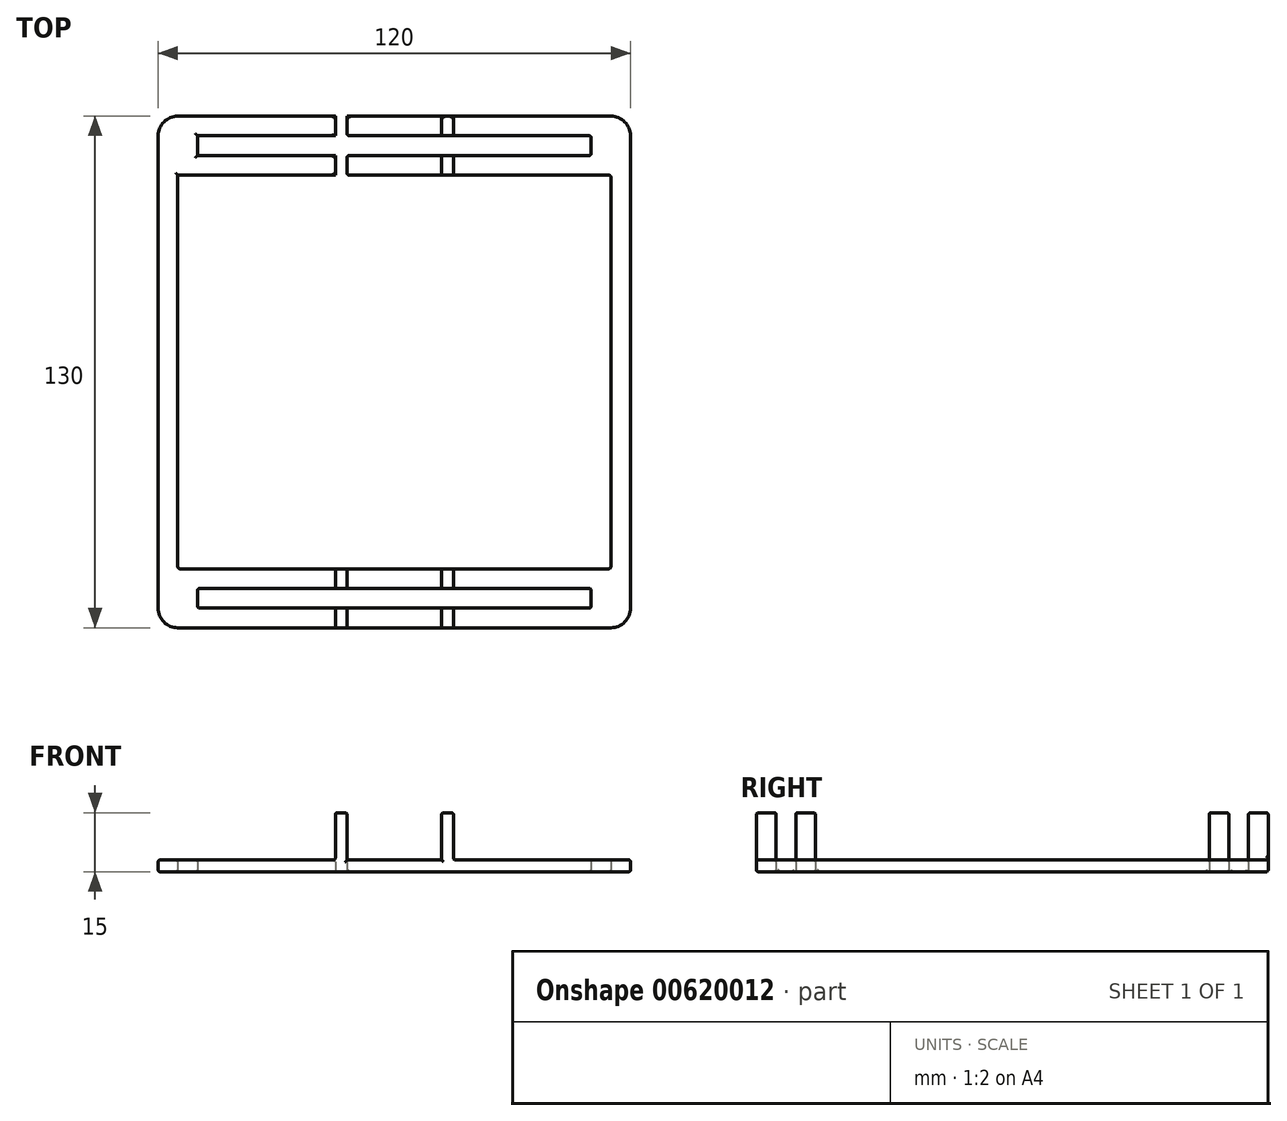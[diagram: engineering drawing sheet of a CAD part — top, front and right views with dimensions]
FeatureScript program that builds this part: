
annotation { "Feature Type Name" : "Feature", "Feature Type Description" : "" }
export const myFeature = defineFeature(function(context is Context, id is Id, definition is map)
    precondition{}
    {
        {
            var Q0;
            Q0=qCreatedBy(makeId("Top.planeOp"),FACE);
            var sketch = newSketch(context, id + "F0", { "sketchPlane" : qUnion([Q0])});
            skLineSegment(sketch, "E0.bottom", {"start": v(-50, 55) * mm, "end": v(50, 55) * mm});
            skLineSegment(sketch, "E0.left", {"start": v(-55, 50) * mm, "end": v(-55, -50) * mm});
            skLineSegment(sketch, "E0.right", {"start": v(55, 50) * mm, "end": v(55, -50) * mm});
            skPoint(sketch, "E0.middle", {"position": v(0, 0) * mm});
            skLineSegment(sketch, "E1.left", {"start": v(-60, 55) * mm, "end": v(-60, -55) * mm});
            skLineSegment(sketch, "E1.right", {"start": v(60, 55) * mm, "end": v(60, -55) * mm});
            skPoint(sketch, "E2.visualSharp", {"position": v(-55, 55) * mm});
            skPoint(sketch, "E3.visualSharp", {"position": v(-60, 60) * mm});
            skPoint(sketch, "E4.visualSharp", {"position": v(55, 55) * mm});
            skPoint(sketch, "E5.visualSharp", {"position": v(60, 60) * mm});
            skPoint(sketch, "E6.visualSharp", {"position": v(55, -55) * mm});
            skPoint(sketch, "E7.visualSharp", {"position": v(60, -60) * mm});
            skPoint(sketch, "E8.visualSharp", {"position": v(-55, -55) * mm});
            skPoint(sketch, "E9.visualSharp", {"position": v(-60, -60) * mm});
            skLineSegment(sketch, "E10", {"start": v(-55, 50) * mm, "end": v(55, 50) * mm});
            skLineSegment(sketch, "E11", {"start": v(-50, 60) * mm, "end": v(-50, 55) * mm});
            skLineSegment(sketch, "E12", {"start": v(50, 60) * mm, "end": v(50, 55) * mm});
            skPoint(sketch, "E13.bottom.end.orphan", {"position": v(15, 55) * mm});
            skPoint(sketch, "E13.bottom.start.orphan", {"position": v(-15, 55) * mm});
            skPoint(sketch, "E13.top.end.orphan", {"position": v(0, 60) * mm});
            skPoint(sketch, "E14.orphan", {"position": v(-15, 60) * mm});
            skPoint(sketch, "E15.orphan", {"position": v(15, 60) * mm});
            skPoint(sketch, "E16.MirrorCS.end.orphan", {"position": v(-15, -60) * mm});
            skPoint(sketch, "E16.MirrorCS.start.orphan", {"position": v(-15, -55) * mm});
            skPoint(sketch, "E17.MirrorCS.end.orphan", {"position": v(15, -60) * mm});
            skPoint(sketch, "E0.top.start.orphan", {"position": v(15, -55) * mm});
            skPoint(sketch, "E1.bottom.start.orphan", {"position": v(-55, 60) * mm});
            skPoint(sketch, "E18.trimOffspring.end.orphan", {"position": v(55, 60) * mm});
            skLineSegment(sketch, "E19", {"start": v(-50, 60) * mm, "end": v(50, 60) * mm});
            skPoint(sketch, "E20", {"position": v(-55, 65) * mm});
            skLineSegment(sketch, "E21", {"start": v(-55, 65) * mm, "end": v(55, 65) * mm});
            skLineSegment(sketch, "E22", {"start": v(-60, 55) * mm, "end": v(-60, 60) * mm});
            skLineSegment(sketch, "E23", {"start": v(-60, 60) * mm, "end": v(-60, 65) * mm});
            skLineSegment(sketch, "E24", {"start": v(-60, 65) * mm, "end": v(-55, 65) * mm});
            skLineSegment(sketch, "E25", {"start": v(60, 55) * mm, "end": v(60, 60) * mm});
            skLineSegment(sketch, "E26", {"start": v(60, 60) * mm, "end": v(60, 65) * mm});
            skLineSegment(sketch, "E27", {"start": v(60, 65) * mm, "end": v(55, 65) * mm});
            skLineSegment(sketch, "E28.MirrorCS", {"start": v(-55, -50) * mm, "end": v(55, -50) * mm});
            skLineSegment(sketch, "E29.MirrorCS", {"start": v(-50, -55) * mm, "end": v(50, -55) * mm});
            skLineSegment(sketch, "E30.MirrorCS", {"start": v(-50, -60) * mm, "end": v(50, -60) * mm});
            skLineSegment(sketch, "E31.MirrorCS", {"start": v(-50, -60) * mm, "end": v(-50, -55) * mm});
            skLineSegment(sketch, "E32.MirrorCS", {"start": v(50, -60) * mm, "end": v(50, -55) * mm});
            skLineSegment(sketch, "E33.MirrorCS", {"start": v(60, -55) * mm, "end": v(60, -60) * mm});
            skLineSegment(sketch, "E34.MirrorCS", {"start": v(60, -60) * mm, "end": v(60, -65) * mm});
            skLineSegment(sketch, "E35.MirrorCS", {"start": v(60, -65) * mm, "end": v(55, -65) * mm});
            skLineSegment(sketch, "E36.MirrorCS", {"start": v(-55, -65) * mm, "end": v(55, -65) * mm});
            skLineSegment(sketch, "E37.MirrorCS", {"start": v(-60, -65) * mm, "end": v(-55, -65) * mm});
            skLineSegment(sketch, "E38.MirrorCS", {"start": v(-60, -60) * mm, "end": v(-60, -65) * mm});
            skLineSegment(sketch, "E39.MirrorCS", {"start": v(-60, -55) * mm, "end": v(-60, -60) * mm});
            skLineSegment(sketch, "E40.bottom", {"start": v(-15, 55) * mm, "end": v(-12, 55) * mm});
            skLineSegment(sketch, "E40.top", {"start": v(-15, 50) * mm, "end": v(-12, 50) * mm});
            skLineSegment(sketch, "E40.left", {"start": v(-15, 55) * mm, "end": v(-15, 50) * mm});
            skLineSegment(sketch, "E40.right", {"start": v(-12, 55) * mm, "end": v(-12, 50) * mm});
            skLineSegment(sketch, "E41.MirrorCS", {"start": v(12, 55) * mm, "end": v(12, 50) * mm});
            skLineSegment(sketch, "E42.MirrorCS", {"start": v(15, 55) * mm, "end": v(15, 50) * mm});
            skLineSegment(sketch, "E43.bottom", {"start": v(-15, 60) * mm, "end": v(-12, 60) * mm});
            skLineSegment(sketch, "E43.top", {"start": v(-15, 65) * mm, "end": v(-12, 65) * mm});
            skLineSegment(sketch, "E43.left", {"start": v(-15, 60) * mm, "end": v(-15, 65) * mm});
            skLineSegment(sketch, "E43.right", {"start": v(-12, 60) * mm, "end": v(-12, 65) * mm});
            skLineSegment(sketch, "E44.MirrorCS", {"start": v(12, 60) * mm, "end": v(12, 65) * mm});
            skLineSegment(sketch, "E45.MirrorCS", {"start": v(15, 60) * mm, "end": v(15, 65) * mm});
            skLineSegment(sketch, "E46.MirrorCS", {"start": v(-15, -55) * mm, "end": v(-15, -50) * mm});
            skLineSegment(sketch, "E47.MirrorCS", {"start": v(-12, -55) * mm, "end": v(-12, -50) * mm});
            skLineSegment(sketch, "E48.MirrorCS", {"start": v(-12, -60) * mm, "end": v(-12, -65) * mm});
            skLineSegment(sketch, "E49.MirrorCS", {"start": v(-15, -60) * mm, "end": v(-15, -65) * mm});
            skLineSegment(sketch, "E50.MirrorCS", {"start": v(12, -60) * mm, "end": v(12, -65) * mm});
            skLineSegment(sketch, "E51.MirrorCS", {"start": v(15, -60) * mm, "end": v(15, -65) * mm});
            skLineSegment(sketch, "E52.MirrorCS", {"start": v(15, -55) * mm, "end": v(15, -50) * mm});
            skLineSegment(sketch, "E53.MirrorCS", {"start": v(12, -55) * mm, "end": v(12, -50) * mm});
            skSolve(sketch);
        }
        {
            var Q0;
            Q0=makeQuery(id+"F0.imprint","IMPRINT",FACE,{"disambiguationData":[TD([[makeQuery(id+"F0.imprint","IMPRINT",EDGE,{"derivedFrom":sQuery(id+"F0.wireOp",EDGE,"E0.left")}),-1.0]])]});
            var Q1;
            Q1=makeQuery(id+"F0.imprint","IMPRINT",FACE,{"disambiguationData":[TD([[makeQuery(id+"F0.imprint","IMPRINT",EDGE,{"derivedFrom":sQuery(id+"F0.wireOp",EDGE,"E0.right")}),1.0]])]});
            extrude(context, id + "F1", {"entities" : qUnion([Q0, Q1]), "depth" : 3 * mm, "offsetDistance" : 25 * mm});
        }
        {
            var Q0;
            Q0=makeQuery(id+"F0.imprint","IMPRINT",FACE,{"disambiguationData":[TD([[makeQuery(id+"F0.imprint","IMPRINT",EDGE,{"derivedFrom":sQuery(id+"F0.wireOp",EDGE,"E43.bottom")}),1.0]])]});
            var Q1;
            Q1=makeQuery(id+"F0.imprint","IMPRINT",FACE,{"disambiguationData":[TD([[makeQuery(id+"F0.imprint","IMPRINT",EDGE,{"derivedFrom":sQuery(id+"F0.wireOp",EDGE,"E40.bottom")}),-1.0]])]});
            var Q2;
            {var subQ0=sQuery(id+"F0.wireOp",EDGE,"E41.MirrorCS");Q2=makeQuery(id+"F0.imprint","IMPRINT",FACE,{"disambiguationData":[TD([[makeQuery(id+"F0.imprint","IMPRINT",EDGE,{"derivedFrom":subQ0}),1.0]])]});}
            var Q3;
            {var subQ0=sQuery(id+"F0.wireOp",EDGE,"E44.MirrorCS");Q3=makeQuery(id+"F0.imprint","IMPRINT",FACE,{"disambiguationData":[TD([[makeQuery(id+"F0.imprint","IMPRINT",EDGE,{"derivedFrom":subQ0}),-1.0]])]});}
            var Q4;
            {var subQ0=sQuery(id+"F0.wireOp",EDGE,"E52.MirrorCS");Q4=makeQuery(id+"F0.imprint","IMPRINT",FACE,{"disambiguationData":[TD([[makeQuery(id+"F0.imprint","IMPRINT",EDGE,{"derivedFrom":subQ0}),1.0]])]});}
            var Q5;
            {var subQ0=sQuery(id+"F0.wireOp",EDGE,"E50.MirrorCS");Q5=makeQuery(id+"F0.imprint","IMPRINT",FACE,{"disambiguationData":[TD([[makeQuery(id+"F0.imprint","IMPRINT",EDGE,{"derivedFrom":subQ0}),1.0]])]});}
            var Q6;
            {var subQ0=sQuery(id+"F0.wireOp",EDGE,"E48.MirrorCS");Q6=makeQuery(id+"F0.imprint","IMPRINT",FACE,{"disambiguationData":[TD([[makeQuery(id+"F0.imprint","IMPRINT",EDGE,{"derivedFrom":subQ0}),-1.0]])]});}
            var Q7;
            {var subQ0=sQuery(id+"F0.wireOp",EDGE,"E46.MirrorCS");Q7=makeQuery(id+"F0.imprint","IMPRINT",FACE,{"disambiguationData":[TD([[makeQuery(id+"F0.imprint","IMPRINT",EDGE,{"derivedFrom":subQ0}),-1.0]])]});}
            extrude(context, id + "F2", {"entities" : qUnion([Q0, Q1, Q2, Q3, Q4, Q5, Q6, Q7]), "depth" : 15 * mm, "offsetDistance" : 25 * mm});
        }
        {
            var Q0;
            {var subQ0=sQuery(id+"F0.wireOp",EDGE,"E43.right");Q0=makeQuery(id+"F0.imprint","IMPRINT",FACE,{"disambiguationData":[TD([[makeQuery(id+"F0.imprint","IMPRINT",EDGE,{"derivedFrom":subQ0}),-1.0]])]});}
            var Q1;
            {var subQ0=sQuery(id+"F0.wireOp",EDGE,"E40.right");Q1=makeQuery(id+"F0.imprint","IMPRINT",FACE,{"disambiguationData":[TD([[makeQuery(id+"F0.imprint","IMPRINT",EDGE,{"derivedFrom":subQ0}),1.0]])]});}
            var Q2;
            {var subQ0=sQuery(id+"F0.wireOp",EDGE,"E47.MirrorCS");Q2=makeQuery(id+"F0.imprint","IMPRINT",FACE,{"disambiguationData":[TD([[makeQuery(id+"F0.imprint","IMPRINT",EDGE,{"derivedFrom":subQ0}),-1.0]])]});}
            var Q3;
            {var subQ0=sQuery(id+"F0.wireOp",EDGE,"E48.MirrorCS");Q3=makeQuery(id+"F0.imprint","IMPRINT",FACE,{"disambiguationData":[TD([[makeQuery(id+"F0.imprint","IMPRINT",EDGE,{"derivedFrom":subQ0}),1.0]])]});}
            extrude(context, id + "F3", {"entities" : qUnion([Q0, Q1, Q2, Q3]), "depth" : 3 * mm, "offsetDistance" : 25 * mm});
        }
        {
            var Q0;
            Q0=makeQuery(id+"F1.opExtrude","SWEPT_BODY",BODY,{"disambiguationData":[OSD([sQuery(id+"F0.wireOp",EDGE,"E0.bottom"),sQuery(id+"F0.wireOp",EDGE,"E0.left"),sQuery(id+"F0.wireOp",EDGE,"E1.left"),sQuery(id+"F0.wireOp",EDGE,"E10"),sQuery(id+"F0.wireOp",EDGE,"E11"),sQuery(id+"F0.wireOp",EDGE,"E19"),sQuery(id+"F0.wireOp",EDGE,"E21"),sQuery(id+"F0.wireOp",EDGE,"E22"),sQuery(id+"F0.wireOp",EDGE,"E23"),sQuery(id+"F0.wireOp",EDGE,"E24"),sQuery(id+"F0.wireOp",EDGE,"E28.MirrorCS"),sQuery(id+"F0.wireOp",EDGE,"E29.MirrorCS"),sQuery(id+"F0.wireOp",EDGE,"E30.MirrorCS"),sQuery(id+"F0.wireOp",EDGE,"E31.MirrorCS"),sQuery(id+"F0.wireOp",EDGE,"E36.MirrorCS"),sQuery(id+"F0.wireOp",EDGE,"E37.MirrorCS"),sQuery(id+"F0.wireOp",EDGE,"E38.MirrorCS"),sQuery(id+"F0.wireOp",EDGE,"E39.MirrorCS"),sQuery(id+"F0.wireOp",EDGE,"E40.left"),sQuery(id+"F0.wireOp",EDGE,"E43.left"),sQuery(id+"F0.wireOp",EDGE,"E46.MirrorCS"),sQuery(id+"F0.wireOp",EDGE,"E49.MirrorCS")])]});
            var Q1;
            Q1=makeQuery(id+"F1.opExtrude","SWEPT_BODY",BODY,{"disambiguationData":[OSD([sQuery(id+"F0.wireOp",EDGE,"E0.bottom"),sQuery(id+"F0.wireOp",EDGE,"E0.right"),sQuery(id+"F0.wireOp",EDGE,"E1.right"),sQuery(id+"F0.wireOp",EDGE,"E10"),sQuery(id+"F0.wireOp",EDGE,"E12"),sQuery(id+"F0.wireOp",EDGE,"E19"),sQuery(id+"F0.wireOp",EDGE,"E21"),sQuery(id+"F0.wireOp",EDGE,"E25"),sQuery(id+"F0.wireOp",EDGE,"E26"),sQuery(id+"F0.wireOp",EDGE,"E27"),sQuery(id+"F0.wireOp",EDGE,"E28.MirrorCS"),sQuery(id+"F0.wireOp",EDGE,"E29.MirrorCS"),sQuery(id+"F0.wireOp",EDGE,"E30.MirrorCS"),sQuery(id+"F0.wireOp",EDGE,"E32.MirrorCS"),sQuery(id+"F0.wireOp",EDGE,"E33.MirrorCS"),sQuery(id+"F0.wireOp",EDGE,"E34.MirrorCS"),sQuery(id+"F0.wireOp",EDGE,"E35.MirrorCS"),sQuery(id+"F0.wireOp",EDGE,"E36.MirrorCS"),sQuery(id+"F0.wireOp",EDGE,"E42.MirrorCS"),sQuery(id+"F0.wireOp",EDGE,"E45.MirrorCS"),sQuery(id+"F0.wireOp",EDGE,"E51.MirrorCS"),sQuery(id+"F0.wireOp",EDGE,"E52.MirrorCS")])]});
            var Q2;
            Q2=makeQuery(id+"F2.opExtrude","SWEPT_BODY",BODY,{"disambiguationData":[OSD([sQuery(id+"F0.wireOp",EDGE,"E0.bottom"),sQuery(id+"F0.wireOp",EDGE,"E10"),sQuery(id+"F0.wireOp",EDGE,"E41.MirrorCS"),sQuery(id+"F0.wireOp",EDGE,"E42.MirrorCS")])]});
            var Q3;
            Q3=makeQuery(id+"F2.opExtrude","SWEPT_BODY",BODY,{"disambiguationData":[OSD([sQuery(id+"F0.wireOp",EDGE,"E19"),sQuery(id+"F0.wireOp",EDGE,"E21"),sQuery(id+"F0.wireOp",EDGE,"E44.MirrorCS"),sQuery(id+"F0.wireOp",EDGE,"E45.MirrorCS")])]});
            var Q4;
            Q4=makeQuery(id+"F2.opExtrude","SWEPT_BODY",BODY,{"disambiguationData":[OSD([sQuery(id+"F0.wireOp",EDGE,"E28.MirrorCS"),sQuery(id+"F0.wireOp",EDGE,"E29.MirrorCS"),sQuery(id+"F0.wireOp",EDGE,"E46.MirrorCS"),sQuery(id+"F0.wireOp",EDGE,"E47.MirrorCS")])]});
            var Q5;
            Q5=makeQuery(id+"F2.opExtrude","SWEPT_BODY",BODY,{"disambiguationData":[OSD([sQuery(id+"F0.wireOp",EDGE,"E28.MirrorCS"),sQuery(id+"F0.wireOp",EDGE,"E29.MirrorCS"),sQuery(id+"F0.wireOp",EDGE,"E52.MirrorCS"),sQuery(id+"F0.wireOp",EDGE,"E53.MirrorCS")])]});
            var Q6;
            Q6=makeQuery(id+"F2.opExtrude","SWEPT_BODY",BODY,{"disambiguationData":[OSD([sQuery(id+"F0.wireOp",EDGE,"E30.MirrorCS"),sQuery(id+"F0.wireOp",EDGE,"E36.MirrorCS"),sQuery(id+"F0.wireOp",EDGE,"E48.MirrorCS"),sQuery(id+"F0.wireOp",EDGE,"E49.MirrorCS")])]});
            var Q7;
            Q7=makeQuery(id+"F2.opExtrude","SWEPT_BODY",BODY,{"disambiguationData":[OSD([sQuery(id+"F0.wireOp",EDGE,"E30.MirrorCS"),sQuery(id+"F0.wireOp",EDGE,"E36.MirrorCS"),sQuery(id+"F0.wireOp",EDGE,"E50.MirrorCS"),sQuery(id+"F0.wireOp",EDGE,"E51.MirrorCS")])]});
            var Q8;
            Q8=makeQuery(id+"F2.opExtrude","SWEPT_BODY",BODY,{"disambiguationData":[OSD([sQuery(id+"F0.wireOp",EDGE,"E40.bottom"),sQuery(id+"F0.wireOp",EDGE,"E40.top"),sQuery(id+"F0.wireOp",EDGE,"E40.left"),sQuery(id+"F0.wireOp",EDGE,"E40.right")])]});
            var Q9;
            Q9=makeQuery(id+"F2.opExtrude","SWEPT_BODY",BODY,{"disambiguationData":[OSD([sQuery(id+"F0.wireOp",EDGE,"E43.bottom"),sQuery(id+"F0.wireOp",EDGE,"E43.top"),sQuery(id+"F0.wireOp",EDGE,"E43.left"),sQuery(id+"F0.wireOp",EDGE,"E43.right")])]});
            var Q10;
            Q10=makeQuery(id+"F3.opExtrude","SWEPT_BODY",BODY,{"disambiguationData":[OSD([sQuery(id+"F0.wireOp",EDGE,"E0.bottom"),sQuery(id+"F0.wireOp",EDGE,"E10"),sQuery(id+"F0.wireOp",EDGE,"E40.right"),sQuery(id+"F0.wireOp",EDGE,"E41.MirrorCS")])]});
            var Q11;
            Q11=makeQuery(id+"F3.opExtrude","SWEPT_BODY",BODY,{"disambiguationData":[OSD([sQuery(id+"F0.wireOp",EDGE,"E19"),sQuery(id+"F0.wireOp",EDGE,"E21"),sQuery(id+"F0.wireOp",EDGE,"E43.right"),sQuery(id+"F0.wireOp",EDGE,"E44.MirrorCS")])]});
            var Q12;
            Q12=makeQuery(id+"F3.opExtrude","SWEPT_BODY",BODY,{"disambiguationData":[OSD([sQuery(id+"F0.wireOp",EDGE,"E28.MirrorCS"),sQuery(id+"F0.wireOp",EDGE,"E29.MirrorCS"),sQuery(id+"F0.wireOp",EDGE,"E47.MirrorCS"),sQuery(id+"F0.wireOp",EDGE,"E53.MirrorCS")])]});
            var Q13;
            Q13=makeQuery(id+"F3.opExtrude","SWEPT_BODY",BODY,{"disambiguationData":[OSD([sQuery(id+"F0.wireOp",EDGE,"E30.MirrorCS"),sQuery(id+"F0.wireOp",EDGE,"E36.MirrorCS"),sQuery(id+"F0.wireOp",EDGE,"E48.MirrorCS"),sQuery(id+"F0.wireOp",EDGE,"E50.MirrorCS")])]});
            booleanBodies(context, id + "F4", {"operationType" : BooleanOperationType.UNION, "tools" : qUnion([Q0, Q1, Q2, Q3, Q4, Q5, Q6, Q7, Q8, Q9, Q10, Q11, Q12, Q13])});
        }
        {
            var Q0;
            Q0=makeQuery(id+"F1.opExtrude","SWEPT_EDGE",EDGE,{"disambiguationData":[OSD([sQuery(id+"F0.wireOp",EDGE,"E34.MirrorCS"),sQuery(id+"F0.wireOp",EDGE,"E35.MirrorCS")])]});
            var Q1;
            Q1=makeQuery(id+"F1.opExtrude","SWEPT_EDGE",EDGE,{"disambiguationData":[OSD([sQuery(id+"F0.wireOp",EDGE,"E26"),sQuery(id+"F0.wireOp",EDGE,"E27")])]});
            var Q2;
            Q2=makeQuery(id+"F1.opExtrude","SWEPT_EDGE",EDGE,{"disambiguationData":[OSD([sQuery(id+"F0.wireOp",EDGE,"E37.MirrorCS"),sQuery(id+"F0.wireOp",EDGE,"E38.MirrorCS")])]});
            var Q3;
            Q3=makeQuery(id+"F1.opExtrude","SWEPT_EDGE",EDGE,{"disambiguationData":[OSD([sQuery(id+"F0.wireOp",EDGE,"E23"),sQuery(id+"F0.wireOp",EDGE,"E24")])]});
            fillet(context, id + "F5", {"entities" : qUnion([Q0, Q1, Q2, Q3]), "radius" : 5 * mm, "tangentPropagation" : true, "allowEdgeOverflow" : false});
        }
        {
            var Q0;
            Q0=makeQuery(id+"F1.opExtrude","CAP_FACE",FACE,{"disambiguationData":[OSD([sQuery(id+"F0.wireOp",EDGE,"E0.bottom"),sQuery(id+"F0.wireOp",EDGE,"E0.left"),sQuery(id+"F0.wireOp",EDGE,"E1.left"),sQuery(id+"F0.wireOp",EDGE,"E10"),sQuery(id+"F0.wireOp",EDGE,"E11"),sQuery(id+"F0.wireOp",EDGE,"E19"),sQuery(id+"F0.wireOp",EDGE,"E21"),sQuery(id+"F0.wireOp",EDGE,"E22"),sQuery(id+"F0.wireOp",EDGE,"E23"),sQuery(id+"F0.wireOp",EDGE,"E24"),sQuery(id+"F0.wireOp",EDGE,"E28.MirrorCS"),sQuery(id+"F0.wireOp",EDGE,"E29.MirrorCS"),sQuery(id+"F0.wireOp",EDGE,"E30.MirrorCS"),sQuery(id+"F0.wireOp",EDGE,"E31.MirrorCS"),sQuery(id+"F0.wireOp",EDGE,"E36.MirrorCS"),sQuery(id+"F0.wireOp",EDGE,"E37.MirrorCS"),sQuery(id+"F0.wireOp",EDGE,"E38.MirrorCS"),sQuery(id+"F0.wireOp",EDGE,"E39.MirrorCS"),sQuery(id+"F0.wireOp",EDGE,"E40.left"),sQuery(id+"F0.wireOp",EDGE,"E43.left"),sQuery(id+"F0.wireOp",EDGE,"E46.MirrorCS"),sQuery(id+"F0.wireOp",EDGE,"E49.MirrorCS")])],"isStart":false});
            var Q1;
            Q1=makeQuery(id+"F1.opExtrude","CAP_FACE",FACE,{"disambiguationData":[OSD([sQuery(id+"F0.wireOp",EDGE,"E0.bottom"),sQuery(id+"F0.wireOp",EDGE,"E0.right"),sQuery(id+"F0.wireOp",EDGE,"E1.right"),sQuery(id+"F0.wireOp",EDGE,"E10"),sQuery(id+"F0.wireOp",EDGE,"E12"),sQuery(id+"F0.wireOp",EDGE,"E19"),sQuery(id+"F0.wireOp",EDGE,"E21"),sQuery(id+"F0.wireOp",EDGE,"E25"),sQuery(id+"F0.wireOp",EDGE,"E26"),sQuery(id+"F0.wireOp",EDGE,"E27"),sQuery(id+"F0.wireOp",EDGE,"E28.MirrorCS"),sQuery(id+"F0.wireOp",EDGE,"E29.MirrorCS"),sQuery(id+"F0.wireOp",EDGE,"E30.MirrorCS"),sQuery(id+"F0.wireOp",EDGE,"E32.MirrorCS"),sQuery(id+"F0.wireOp",EDGE,"E33.MirrorCS"),sQuery(id+"F0.wireOp",EDGE,"E34.MirrorCS"),sQuery(id+"F0.wireOp",EDGE,"E35.MirrorCS"),sQuery(id+"F0.wireOp",EDGE,"E36.MirrorCS"),sQuery(id+"F0.wireOp",EDGE,"E42.MirrorCS"),sQuery(id+"F0.wireOp",EDGE,"E45.MirrorCS"),sQuery(id+"F0.wireOp",EDGE,"E51.MirrorCS"),sQuery(id+"F0.wireOp",EDGE,"E52.MirrorCS")])],"isStart":false});
            var Q2;
            {var subQ0=sQuery(id+"F0.wireOp",EDGE,"E36.MirrorCS");Q2=makeQuery(id+"F4.opBoolean","MERGE",FACE,{"derivedFrom":[makeQuery(id+"F1.opExtrude","SWEPT_FACE",FACE,{"disambiguationData":[OSD([sQuery(id+"F0.wireOp",EDGE,"E35.MirrorCS"),subQ0])]}),makeQuery(id+"F1.opExtrude","SWEPT_FACE",FACE,{"disambiguationData":[OSD([subQ0,sQuery(id+"F0.wireOp",EDGE,"E37.MirrorCS")])]}),makeQuery(id+"F2.opExtrude","SWEPT_FACE",FACE,{"disambiguationData":[OSD([subQ0]),TDD([makeQuery(id+"F0.imprint","IMPRINT",EDGE,{"disambiguationData":[TD([[makeQuery(id+"F0.imprint","INTERSECT",VERTEX,{"derivedFrom":[subQ0,sQuery(id+"F0.wireOp",EDGE,"E48.MirrorCS")]}),1.0]])],"derivedFrom":subQ0})])]}),makeQuery(id+"F2.opExtrude","SWEPT_FACE",FACE,{"disambiguationData":[OSD([subQ0]),TDD([makeQuery(id+"F0.imprint","IMPRINT",EDGE,{"disambiguationData":[TD([[makeQuery(id+"F0.imprint","INTERSECT",VERTEX,{"derivedFrom":[subQ0,sQuery(id+"F0.wireOp",EDGE,"E50.MirrorCS")]}),-1.0]])],"derivedFrom":subQ0})])]}),makeQuery(id+"F3.opExtrude","SWEPT_FACE",FACE,{"disambiguationData":[OSD([subQ0])]})]});}
            var Q3;
            {var subQ0=sQuery(id+"F0.wireOp",EDGE,"E29.MirrorCS");var subQ1=makeQuery(id+"F0.imprint","INTERSECT",VERTEX,{"derivedFrom":[subQ0,sQuery(id+"F0.wireOp",EDGE,"E52.MirrorCS")]});var subQ2=makeQuery(id+"F0.imprint","INTERSECT",VERTEX,{"derivedFrom":[subQ0,sQuery(id+"F0.wireOp",EDGE,"E46.MirrorCS")]});Q3=makeQuery(id+"F4.opBoolean","MERGE",FACE,{"derivedFrom":[makeQuery(id+"F1.opExtrude","SWEPT_FACE",FACE,{"disambiguationData":[OSD([subQ0]),TDD([makeQuery(id+"F0.imprint","IMPRINT",EDGE,{"disambiguationData":[TD([[makeQuery(id+"F0.imprint","INTERSECT",VERTEX,{"derivedFrom":[subQ0,sQuery(id+"F0.wireOp",EDGE,"E31.MirrorCS")]}),-1.0]])],"derivedFrom":subQ0})])]}),makeQuery(id+"F1.opExtrude","SWEPT_FACE",FACE,{"disambiguationData":[OSD([subQ0]),TDD([makeQuery(id+"F0.imprint","IMPRINT",EDGE,{"disambiguationData":[TD([[makeQuery(id+"F0.imprint","INTERSECT",VERTEX,{"derivedFrom":[subQ0,sQuery(id+"F0.wireOp",EDGE,"E32.MirrorCS")]}),1.0]])],"derivedFrom":subQ0})])]}),makeQuery(id+"F2.opExtrude","SWEPT_FACE",FACE,{"disambiguationData":[OSD([subQ0]),TDD([makeQuery(id+"F0.imprint","IMPRINT",EDGE,{"disambiguationData":[TD([[subQ2,-1.0]])],"derivedFrom":subQ0})])]}),makeQuery(id+"F2.opExtrude","SWEPT_FACE",FACE,{"disambiguationData":[OSD([subQ0]),TDD([makeQuery(id+"F0.imprint","IMPRINT",EDGE,{"disambiguationData":[TD([[subQ1,1.0]])],"derivedFrom":subQ0})])]}),makeQuery(id+"F3.opExtrude","SWEPT_FACE",FACE,{"disambiguationData":[OSD([subQ0])]})]});}
            var Q4;
            {var subQ0=sQuery(id+"F0.wireOp",EDGE,"E30.MirrorCS");Q4=makeQuery(id+"F4.opBoolean","MERGE",FACE,{"derivedFrom":[makeQuery(id+"F1.opExtrude","SWEPT_FACE",FACE,{"disambiguationData":[OSD([subQ0]),TDD([makeQuery(id+"F0.imprint","IMPRINT",EDGE,{"disambiguationData":[TD([[makeQuery(id+"F0.imprint","INTERSECT",VERTEX,{"derivedFrom":[subQ0,sQuery(id+"F0.wireOp",EDGE,"E31.MirrorCS")]}),-1.0]])],"derivedFrom":subQ0})])]}),makeQuery(id+"F1.opExtrude","SWEPT_FACE",FACE,{"disambiguationData":[OSD([subQ0]),TDD([makeQuery(id+"F0.imprint","IMPRINT",EDGE,{"disambiguationData":[TD([[makeQuery(id+"F0.imprint","INTERSECT",VERTEX,{"derivedFrom":[subQ0,sQuery(id+"F0.wireOp",EDGE,"E32.MirrorCS")]}),1.0]])],"derivedFrom":subQ0})])]}),makeQuery(id+"F2.opExtrude","SWEPT_FACE",FACE,{"disambiguationData":[OSD([subQ0]),TDD([makeQuery(id+"F0.imprint","IMPRINT",EDGE,{"disambiguationData":[TD([[makeQuery(id+"F0.imprint","INTERSECT",VERTEX,{"derivedFrom":[subQ0,sQuery(id+"F0.wireOp",EDGE,"E48.MirrorCS")]}),1.0]])],"derivedFrom":subQ0})])]}),makeQuery(id+"F2.opExtrude","SWEPT_FACE",FACE,{"disambiguationData":[OSD([subQ0]),TDD([makeQuery(id+"F0.imprint","IMPRINT",EDGE,{"disambiguationData":[TD([[makeQuery(id+"F0.imprint","INTERSECT",VERTEX,{"derivedFrom":[subQ0,sQuery(id+"F0.wireOp",EDGE,"E50.MirrorCS")]}),-1.0]])],"derivedFrom":subQ0})])]}),makeQuery(id+"F3.opExtrude","SWEPT_FACE",FACE,{"disambiguationData":[OSD([subQ0])]})]});}
            var Q5;
            {var subQ0=sQuery(id+"F0.wireOp",EDGE,"E10");var subQ1=sQuery(id+"F0.wireOp",EDGE,"E40.top");Q5=makeQuery(id+"F4.opBoolean","MERGE",FACE,{"derivedFrom":[makeQuery(id+"F1.opExtrude","SWEPT_FACE",FACE,{"disambiguationData":[OSD([subQ0]),TDD([makeQuery(id+"F0.imprint","IMPRINT",EDGE,{"disambiguationData":[TD([[makeQuery(id+"F0.imprint","INTERSECT",VERTEX,{"derivedFrom":[sQuery(id+"F0.wireOp",EDGE,"E0.left"),subQ0]}),-1.0]])],"derivedFrom":subQ0})])]}),makeQuery(id+"F1.opExtrude","SWEPT_FACE",FACE,{"disambiguationData":[OSD([subQ0]),TDD([makeQuery(id+"F0.imprint","IMPRINT",EDGE,{"disambiguationData":[TD([[makeQuery(id+"F0.imprint","INTERSECT",VERTEX,{"derivedFrom":[sQuery(id+"F0.wireOp",EDGE,"E0.right"),subQ0]}),1.0]])],"derivedFrom":subQ0})])]}),makeQuery(id+"F2.opExtrude","SWEPT_FACE",FACE,{"disambiguationData":[OSD([subQ0])]}),makeQuery(id+"F2.opExtrude","SWEPT_FACE",FACE,{"disambiguationData":[OSD([subQ1])]}),makeQuery(id+"F3.opExtrude","SWEPT_FACE",FACE,{"disambiguationData":[OSD([subQ0])]})]});}
            var Q6;
            {var subQ0=sQuery(id+"F0.wireOp",EDGE,"E19");var subQ1=sQuery(id+"F0.wireOp",EDGE,"E43.bottom");Q6=makeQuery(id+"F4.opBoolean","MERGE",FACE,{"derivedFrom":[makeQuery(id+"F1.opExtrude","SWEPT_FACE",FACE,{"disambiguationData":[OSD([subQ0]),TDD([makeQuery(id+"F0.imprint","IMPRINT",EDGE,{"disambiguationData":[TD([[makeQuery(id+"F0.imprint","INTERSECT",VERTEX,{"derivedFrom":[sQuery(id+"F0.wireOp",EDGE,"E11"),subQ0]}),-1.0]])],"derivedFrom":subQ0})])]}),makeQuery(id+"F1.opExtrude","SWEPT_FACE",FACE,{"disambiguationData":[OSD([subQ0]),TDD([makeQuery(id+"F0.imprint","IMPRINT",EDGE,{"disambiguationData":[TD([[makeQuery(id+"F0.imprint","INTERSECT",VERTEX,{"derivedFrom":[sQuery(id+"F0.wireOp",EDGE,"E12"),subQ0]}),1.0]])],"derivedFrom":subQ0})])]}),makeQuery(id+"F2.opExtrude","SWEPT_FACE",FACE,{"disambiguationData":[OSD([subQ0])]}),makeQuery(id+"F2.opExtrude","SWEPT_FACE",FACE,{"disambiguationData":[OSD([subQ1])]}),makeQuery(id+"F3.opExtrude","SWEPT_FACE",FACE,{"disambiguationData":[OSD([subQ0])]})]});}
            var Q7;
            {var subQ0=sQuery(id+"F0.wireOp",EDGE,"E0.bottom");var subQ1=sQuery(id+"F0.wireOp",EDGE,"E40.bottom");Q7=makeQuery(id+"F4.opBoolean","MERGE",FACE,{"derivedFrom":[makeQuery(id+"F1.opExtrude","SWEPT_FACE",FACE,{"disambiguationData":[OSD([subQ0]),TDD([makeQuery(id+"F0.imprint","IMPRINT",EDGE,{"disambiguationData":[TD([[makeQuery(id+"F0.imprint","INTERSECT",VERTEX,{"derivedFrom":[subQ0,sQuery(id+"F0.wireOp",EDGE,"E11")]}),-1.0]])],"derivedFrom":subQ0})])]}),makeQuery(id+"F1.opExtrude","SWEPT_FACE",FACE,{"disambiguationData":[OSD([subQ0]),TDD([makeQuery(id+"F0.imprint","IMPRINT",EDGE,{"disambiguationData":[TD([[makeQuery(id+"F0.imprint","INTERSECT",VERTEX,{"derivedFrom":[subQ0,sQuery(id+"F0.wireOp",EDGE,"E12")]}),1.0]])],"derivedFrom":subQ0})])]}),makeQuery(id+"F2.opExtrude","SWEPT_FACE",FACE,{"disambiguationData":[OSD([subQ0])]}),makeQuery(id+"F2.opExtrude","SWEPT_FACE",FACE,{"disambiguationData":[OSD([subQ1])]}),makeQuery(id+"F3.opExtrude","SWEPT_FACE",FACE,{"disambiguationData":[OSD([subQ0])]})]});}
            var Q8;
            Q8=makeQuery(id+"F3.opExtrude","CAP_FACE",FACE,{"disambiguationData":[OSD([sQuery(id+"F0.wireOp",EDGE,"E19"),sQuery(id+"F0.wireOp",EDGE,"E21"),sQuery(id+"F0.wireOp",EDGE,"E43.right"),sQuery(id+"F0.wireOp",EDGE,"E44.MirrorCS")])],"isStart":false});
            var Q9;
            Q9=makeQuery(id+"F3.opExtrude","CAP_FACE",FACE,{"disambiguationData":[OSD([sQuery(id+"F0.wireOp",EDGE,"E0.bottom"),sQuery(id+"F0.wireOp",EDGE,"E10"),sQuery(id+"F0.wireOp",EDGE,"E40.right"),sQuery(id+"F0.wireOp",EDGE,"E41.MirrorCS")])],"isStart":false});
            var Q10;
            Q10=makeQuery(id+"F3.opExtrude","CAP_FACE",FACE,{"disambiguationData":[OSD([sQuery(id+"F0.wireOp",EDGE,"E28.MirrorCS"),sQuery(id+"F0.wireOp",EDGE,"E29.MirrorCS"),sQuery(id+"F0.wireOp",EDGE,"E47.MirrorCS"),sQuery(id+"F0.wireOp",EDGE,"E53.MirrorCS")])],"isStart":false});
            var Q11;
            {var subQ0=sQuery(id+"F0.wireOp",EDGE,"E28.MirrorCS");var subQ1=makeQuery(id+"F0.imprint","INTERSECT",VERTEX,{"derivedFrom":[subQ0,sQuery(id+"F0.wireOp",EDGE,"E52.MirrorCS")]});var subQ2=makeQuery(id+"F0.imprint","INTERSECT",VERTEX,{"derivedFrom":[subQ0,sQuery(id+"F0.wireOp",EDGE,"E46.MirrorCS")]});Q11=makeQuery(id+"F4.opBoolean","MERGE",FACE,{"derivedFrom":[makeQuery(id+"F1.opExtrude","SWEPT_FACE",FACE,{"disambiguationData":[OSD([subQ0]),TDD([makeQuery(id+"F0.imprint","IMPRINT",EDGE,{"disambiguationData":[TD([[makeQuery(id+"F0.imprint","INTERSECT",VERTEX,{"derivedFrom":[sQuery(id+"F0.wireOp",EDGE,"E0.left"),subQ0]}),-1.0]])],"derivedFrom":subQ0})])]}),makeQuery(id+"F1.opExtrude","SWEPT_FACE",FACE,{"disambiguationData":[OSD([subQ0]),TDD([makeQuery(id+"F0.imprint","IMPRINT",EDGE,{"disambiguationData":[TD([[makeQuery(id+"F0.imprint","INTERSECT",VERTEX,{"derivedFrom":[sQuery(id+"F0.wireOp",EDGE,"E0.right"),subQ0]}),1.0]])],"derivedFrom":subQ0})])]}),makeQuery(id+"F2.opExtrude","SWEPT_FACE",FACE,{"disambiguationData":[OSD([subQ0]),TDD([makeQuery(id+"F0.imprint","IMPRINT",EDGE,{"disambiguationData":[TD([[subQ2,-1.0]])],"derivedFrom":subQ0})])]}),makeQuery(id+"F2.opExtrude","SWEPT_FACE",FACE,{"disambiguationData":[OSD([subQ0]),TDD([makeQuery(id+"F0.imprint","IMPRINT",EDGE,{"disambiguationData":[TD([[subQ1,1.0]])],"derivedFrom":subQ0})])]}),makeQuery(id+"F3.opExtrude","SWEPT_FACE",FACE,{"disambiguationData":[OSD([subQ0])]})]});}
            var Q12;
            Q12=makeQuery(id+"F2.opExtrude","CAP_FACE",FACE,{"disambiguationData":[OSD([sQuery(id+"F0.wireOp",EDGE,"E28.MirrorCS"),sQuery(id+"F0.wireOp",EDGE,"E29.MirrorCS"),sQuery(id+"F0.wireOp",EDGE,"E52.MirrorCS"),sQuery(id+"F0.wireOp",EDGE,"E53.MirrorCS")])],"isStart":false});
            var Q13;
            Q13=makeQuery(id+"F2.opExtrude","CAP_FACE",FACE,{"disambiguationData":[OSD([sQuery(id+"F0.wireOp",EDGE,"E30.MirrorCS"),sQuery(id+"F0.wireOp",EDGE,"E36.MirrorCS"),sQuery(id+"F0.wireOp",EDGE,"E50.MirrorCS"),sQuery(id+"F0.wireOp",EDGE,"E51.MirrorCS")])],"isStart":false});
            var Q14;
            Q14=makeQuery(id+"F2.opExtrude","CAP_FACE",FACE,{"disambiguationData":[OSD([sQuery(id+"F0.wireOp",EDGE,"E30.MirrorCS"),sQuery(id+"F0.wireOp",EDGE,"E36.MirrorCS"),sQuery(id+"F0.wireOp",EDGE,"E48.MirrorCS"),sQuery(id+"F0.wireOp",EDGE,"E49.MirrorCS")])],"isStart":false});
            var Q15;
            Q15=makeQuery(id+"F2.opExtrude","CAP_FACE",FACE,{"disambiguationData":[OSD([sQuery(id+"F0.wireOp",EDGE,"E28.MirrorCS"),sQuery(id+"F0.wireOp",EDGE,"E29.MirrorCS"),sQuery(id+"F0.wireOp",EDGE,"E46.MirrorCS"),sQuery(id+"F0.wireOp",EDGE,"E47.MirrorCS")])],"isStart":false});
            var Q16;
            Q16=makeQuery(id+"F2.opExtrude","CAP_FACE",FACE,{"disambiguationData":[OSD([sQuery(id+"F0.wireOp",EDGE,"E43.bottom"),sQuery(id+"F0.wireOp",EDGE,"E43.top"),sQuery(id+"F0.wireOp",EDGE,"E43.left"),sQuery(id+"F0.wireOp",EDGE,"E43.right")])],"isStart":false});
            var Q17;
            Q17=makeQuery(id+"F2.opExtrude","CAP_FACE",FACE,{"disambiguationData":[OSD([sQuery(id+"F0.wireOp",EDGE,"E40.bottom"),sQuery(id+"F0.wireOp",EDGE,"E40.top"),sQuery(id+"F0.wireOp",EDGE,"E40.left"),sQuery(id+"F0.wireOp",EDGE,"E40.right")])],"isStart":false});
            var Q18;
            Q18=makeQuery(id+"F2.opExtrude","CAP_FACE",FACE,{"disambiguationData":[OSD([sQuery(id+"F0.wireOp",EDGE,"E0.bottom"),sQuery(id+"F0.wireOp",EDGE,"E10"),sQuery(id+"F0.wireOp",EDGE,"E41.MirrorCS"),sQuery(id+"F0.wireOp",EDGE,"E42.MirrorCS")])],"isStart":false});
            var Q19;
            Q19=makeQuery(id+"F2.opExtrude","CAP_FACE",FACE,{"disambiguationData":[OSD([sQuery(id+"F0.wireOp",EDGE,"E19"),sQuery(id+"F0.wireOp",EDGE,"E21"),sQuery(id+"F0.wireOp",EDGE,"E44.MirrorCS"),sQuery(id+"F0.wireOp",EDGE,"E45.MirrorCS")])],"isStart":false});
            fillet(context, id + "F6", {"entities" : qUnion([Q0, Q1, Q2, Q3, Q4, Q5, Q6, Q7, Q8, Q9, Q10, Q11, Q12, Q13, Q14, Q15, Q16, Q17, Q18, Q19]), "radius" : 0.5 * mm, "tangentPropagation" : true, "allowEdgeOverflow" : false});
        }
    });
